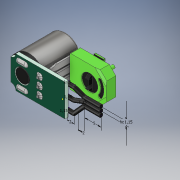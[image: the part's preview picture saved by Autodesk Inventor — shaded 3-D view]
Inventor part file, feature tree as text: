
AUTODESK INVENTOR PART (.ipt)
format: ipt  version: 2019 (Build 230136000, 136)  size: 1,271,808 bytes
history: native  units: mm
features: extrude x28, sketch x24, fillet x12, projected_geometry x9, plane x8, chamfer x8, reference x4, mirror x3, sweep x3, other x3, pattern_linear x2
ambient origin geometry x8: Origin, YZ Plane, XZ Plane, XY Plane, X Axis, Y Axis, Z Axis, Center Point
bodies: Solid1 (feature_tree)
feature tree (104):
  extrude  "Extrusion1"  Depth=9.75mm
  extrude  "Extrusion2"  Depth=3.5mm
  sketch  "Sketch3"  dims[d4=4.0mm d5=4.5mm]
  extrude  "Extrusion3"  Depth=4.5mm
  extrude  "Extrusion4"  Depth=10.0mm
  extrude  "Extrusion5"  Depth=12.25mm TaperAngle=0.0deg
  extrude  "Extrusion6"  Depth=0.75mm
  extrude  "Extrusion7"  Depth=0.5mm TaperAngle=0.0deg
  sketch  "Sketch6"  dims[d12=4.0mm d13=0.75mm]
  extrude  "Extrusion8"  Depth=6.5mm
  extrude  "Extrusion9"  Depth=1.5mm
  extrude  "Extrusion11"  Depth=1.0mm TaperAngle=0.0deg
  fillet  "Fillet2"  Radius=0.6mm
  fillet  "Fillet3"  Radius=4.5mm
  plane  "Work Plane1"
  mirror  "Mirror1"
  fillet  "Fillet4"  Radius=3.4mm
  extrude  "Extrusion12"  Depth=0.25mm TaperAngle=0.0deg
  chamfer  "Chamfer1"  Distance=1.0mm
  chamfer  "Chamfer2"  Distance=0.75mm
  chamfer  "Chamfer3"  Distance=0.25mm
  chamfer  "Chamfer4"  Distance=0.25mm
  plane  "Work Plane2"
  extrude  "Extrusion13"  Depth=0.25mm
  fillet  "Fillet6"  Radius=0.4mm
  pattern_linear  "Rectangular Pattern1"  Spacing1=4.0mm  [1 undecoded]
  mirror  "Mirror2"
  extrude  "Extrusion14"  Depth=0.5mm
  fillet  "Fillet8"  Radius=1.5mm
  plane  "Work Plane3"
  extrude  "Extrusion15"  Depth=0.5mm TaperAngle=0.0deg
  fillet  "Fillet9"  Radius=0.25mm
  pattern_linear  "Rectangular Pattern2"  Spacing1=0.25mm  [1 undecoded]
  fillet  "Fillet10"  Radius=0.25mm
  fillet  "Fillet11"  Radius=0.25mm
  plane  "Work Plane4"
  extrude  "Extrusion16"  [1 undecoded]
  fillet  "Fillet12"  Radius=0.4mm
  chamfer  "Chamfer5"  Distance=2.0mm
  chamfer  "Chamfer6"  Distance=0.05mm
  sketch  "Sketch13"  dims[d36=1.5mm]
  extrude  "Extrusion17"  Depth=0.5mm TaperAngle=0.0deg
  extrude  "Extrusion18"  Depth=0.5mm
  sketch  "Sketch14"  dims[d37=2.25mm]
  extrude  "Extrusion19"  Depth=0.5mm
  extrude  "Extrusion20"  Depth=0.5mm
  sketch  "Sketch15"  dims[d39=2.0mm d40=0.75mm d41=0.0mm d42=0.25mm d43=0.0mm d50=0.25mm d51=0.0mm]
  extrude  "Extrusion21"  Depth=0.5mm
  extrude  "Extrusion22"  Depth=0.5mm
  extrude  "Extrusion23"  Depth=0.5mm
  extrude  "Extrusion24"  Depth=0.5mm TaperAngle=0.0deg
  plane  "Work Plane5"
  extrude  "Extrusion26"  Depth=0.5mm
  chamfer  "Chamfer7"  [1 undecoded]
  fillet  "Fillet13"  Radius=0.75mm
  mirror  "Mirror3"
  extrude  "Extrusion27"  Depth=0.5mm
  chamfer  "Chamfer8"  Distance=2.0mm
  fillet  "Fillet14"  Radius=2.0mm
  sketch  "Sketch19"  dims[d58=0.1mm]
  extrude  "Extrusion30"  Depth=0.5mm
  extrude  "Extrusion31"  Depth=0.5mm
  plane  "Work Plane7"
  sketch  "Sketch23"  dims[d61=0.5mm]
  plane  "Work Plane8"
  sketch  "Sketch24"  dims[d62=0.05mm]
  sketch  "3D Sketch2"
  plane  "Work Plane9"
  sketch  "Sketch25"  dims[d63=0.1mm d64=0.15mm d66=4.0mm d67=5.0mm d68=1.5mm d69=1.5mm d70=0.0mm d71=0.25mm d72=0.75mm d73=45.0deg d74=0.25mm d75=0.75mm d76=45.0deg d77=0.25mm d78=0.75mm d79=45.0deg d80=0.25mm d81=0.75mm d82=45.0deg d83=-0.5mm d84=0.4mm d85=2.0mm d86=0.05mm d87=0.5mm d88=0.0mm d89=0.5mm d90=0.25mm d92=40.0mm d94=1.333333mm d95=1.5mm d96=7.0mm d97=3.5mm d98=2.0mm d99=0.5mm d100=0.0mm d101=0.7mm d102=-7.75mm d103=0.75mm d104=1.65mm d105=2.0mm d106=2.0mm d107=9.0mm d108=2.0mm d109=0.75mm d110=0.5mm d111=0.0mm d112=2.0mm d113=30.0mm d115=2.5mm d116=0.1mm d117=0.6mm d118=0.25mm d119=7.5mm d120=9.6mm d121=11.0mm d122=2.0mm d123=2.0mm d124=2.0mm d125=2.0mm d126=3.0mm d127=0.0mm d128=0.5mm d129=0.25mm d130=1.0mm d131=45.0deg d132=0.25mm d133=1.0mm d134=45.0deg d135=5.0mm d137=1.1mm d138=4.25mm d139=0.75mm d140=0.25mm d141=0.0mm d142=0.25mm d143=0.0mm d144=8.25mm d145=0.05mm d146=0.5mm d148=5.0mm d149=1.0mm d150=0.0mm d151=2.5mm d152=0.0mm d153=6.5mm d154=5.75mm d155=2.5mm d156=1.0mm d157=0.25mm d158=0.25mm d159=0.3mm d160=0.3mm d161=0.6mm d162=0.55mm d163=0.15mm d164=0.0mm d165=0.1mm d166=0.0mm d167=0.1mm d168=0.0mm d169=0.5mm d170=0.0mm d177=0.5mm d182=-5.5mm d185=0.5mm d186=0.5mm d187=0.5mm d188=0.1mm d189=3.0mm d190=0.0mm d191=0.5mm d192=0.5mm d193=45.0deg d194=0.1mm d195=0.75mm d196=1.0mm d197=0.0mm d198=0.5mm d199=0.5mm d200=45.0deg d202=0.1mm d203=0.25mm d204=3.5mm d205=0.75mm d206=1.0mm d228=0.5mm d229=6.0mm d230=0.5mm d231=0.4mm d232=0.0mm d233=0.3mm d234=0.3mm d235=0.25mm d236=1.0mm d237=1.0mm d238=1.0mm d239=0.5mm d240=0.5mm d241=1.0mm d242=0.0mm d243=0.5mm d244=2.0mm d245=1.75mm d246=1.15mm d247=1.15mm d248=2.0mm d249=5.0mm d250=1.15mm d251=1.15mm d252=1.15mm d253=0.0mm d254=0.0mm d255=0.0mm d256=0.0mm d257=0.0mm d258=0.0mm d259=0.5mm d260=0.5mm d261=0.0mm]
  sweep  "Sweep4"
  sweep  "Sweep5"
  sweep  "Sweep6"
  fillet  "Fillet17"  Radius=30.0mm
  extrude  "Extrusion32"  Depth=0.5mm
  sketch  "Sketch1"  dims[d0=16.5mm d1=9.75mm]
  sketch  "Sketch2"  dims[d2=3.0mm d3=3.5mm]
  sketch  "Sketch4"  dims[d6=1.0mm d7=0.0mm d8=10.0mm]
  sketch  "Sketch5"  dims[d9=8.0mm d10=12.25mm d11=0.0mm]
  projected_geometry  "Projected Loop1"
  sketch  "Sketch7"  dims[d14=0.5mm d15=0.0mm d16=3.0mm d17=0.0mm]
  sketch  "Sketch8"  dims[d18=1.0mm d19=6.5mm]
  sketch  "Sketch9"  dims[d20=1.25mm d21=1.5mm]
  sketch  "Sketch10"  dims[d22=1.75mm d24=1.0mm d25=0.0mm d26=0.6mm d27=4.5mm d28=3.4mm]
  projected_geometry  "Projected Loop2"
  projected_geometry  "Projected Loop3"
  sketch  "Sketch11"  dims[d30=6.5mm d31=0.25mm d32=0.0mm]
  sketch  "Sketch12"  dims[d33=0.01mm d34=1.0mm d35=0.0mm]
  projected_geometry  "Projected Loop4"
  projected_geometry  "Projected Loop5"
  projected_geometry  "Projected Loop6"
  sketch  "Sketch17"  dims[d54=0.1mm d55=0.25mm d56=0.4mm]
  projected_geometry  "Projected Loop7"
  sketch  "Sketch18"  dims[d57=0.75mm]
  sketch  "Sketch21"  dims[d59=1.25mm]
  sketch  "Sketch22"  dims[d60=0.25mm]
  reference  "Reference1"
  reference  "Reference2"
  reference  "Reference3"
  reference  "Reference4"
  projected_geometry  "Project Cut Edges1"
  projected_geometry  "Project Cut Edges3"
  other  "<userpath>\OneDrive\Documenten\Inventor\servo\Assembly1.iam"
  other  "Assembly1.iam"
  other  "servo midden:1"
note: 4 required parameter values undecoded (feature->parameter linkage not recoverable at this tier; creation-order binding heuristic only, values carry confidence <= 0.55)
